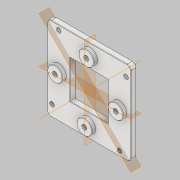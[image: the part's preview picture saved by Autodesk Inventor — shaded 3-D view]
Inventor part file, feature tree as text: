
AUTODESK INVENTOR PART (.ipt)
format: ipt  version: 2019.2 (Build 232265000, 265)  size: 472,064 bytes
history: native  units: mm
features: plane x4, sketch x3, extrude x2, fillet x2, other x1
ambient origin geometry x8: Origin, YZ Plane, XZ Plane, XY Plane, X Axis, Y Axis, Z Axis, Center Point
bodies: Volumenkörper1 (feature_tree)
feature tree (12):
  other  "BaseBottom"
  sketch  "Skizze3"  dims[d3=2.1mm d4=2.1mm d5=2.1mm d6=5.5mm]
  extrude  "Extrusion1"  Depth=5.5mm
  extrude  "Extrusion3"  Depth=5.5mm
  fillet  "Rundung1"  Radius=2.1mm
  plane  "Arbeitsebene1"
  plane  "Arbeitsebene2"
  plane  "Arbeitsebene3"
  plane  "Arbeitsebene4"
  fillet  "Rundung2"  Radius=5.5mm
  sketch  "Skizze2"  dims[d0=10.0mm d2=5.5mm]
  sketch  "Skizze6"  dims[d7=5.5mm d8=5.5mm d9=3.0mm d10=0.0mm d18=8.0mm d19=2.0mm d20=0.0mm d21=2.0mm d22=0.25mm]
